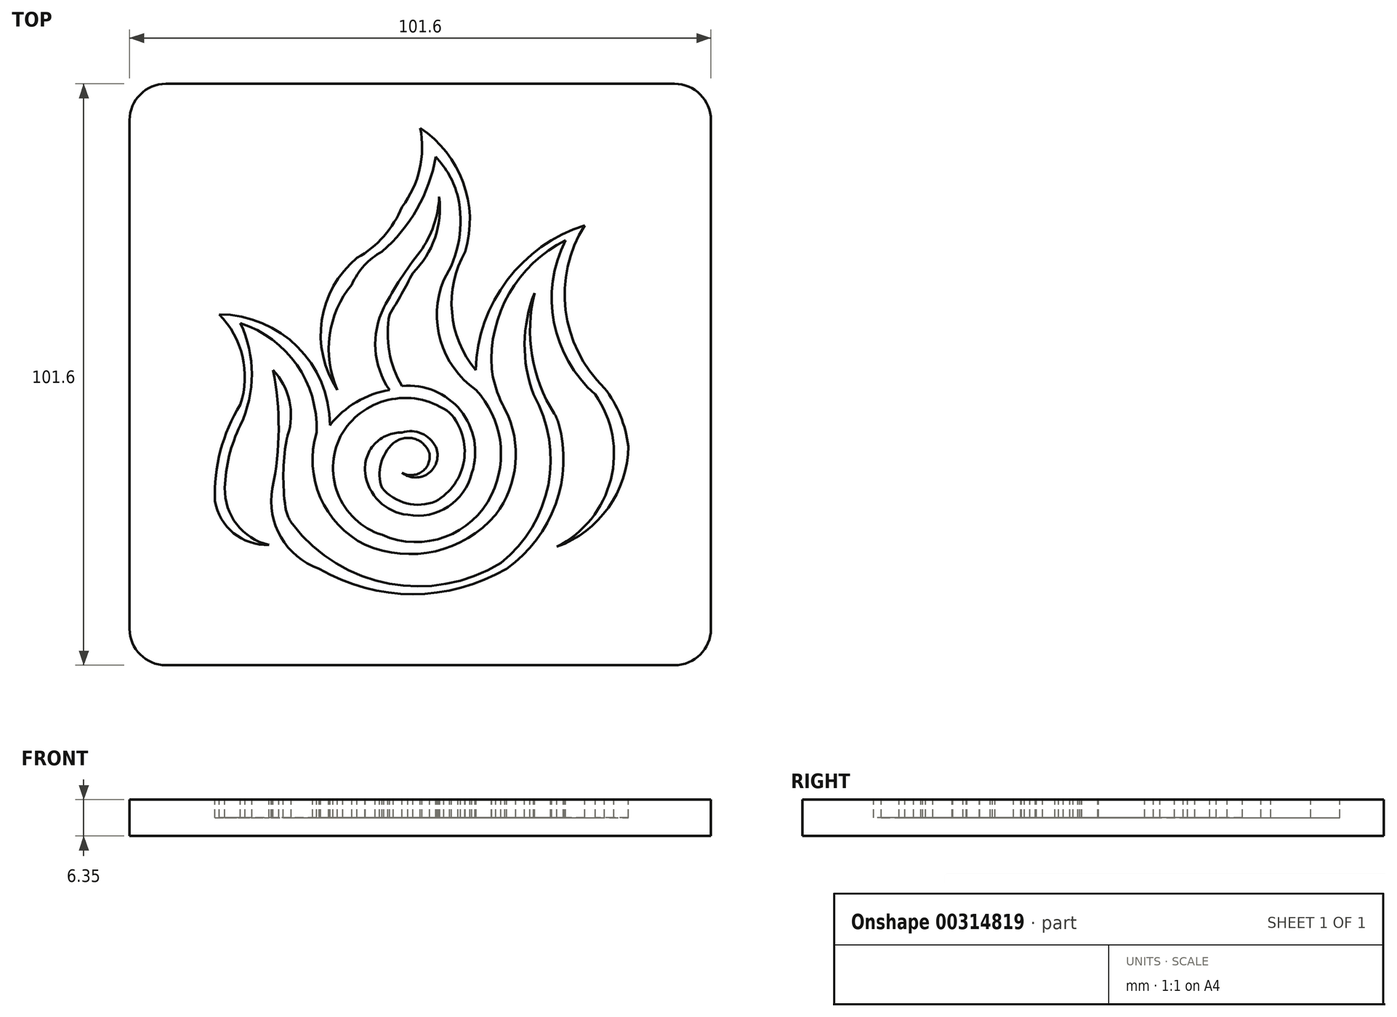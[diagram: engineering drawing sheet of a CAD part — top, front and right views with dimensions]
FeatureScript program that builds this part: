
annotation { "Feature Type Name" : "Feature", "Feature Type Description" : "" }
export const myFeature = defineFeature(function(context is Context, id is Id, definition is map)
    precondition{}
    {
        {
            var Q0;
            Q0=qCreatedBy(makeId("Top.planeOp"),FACE);
            var sketch = newSketch(context, id + "F0", { "sketchPlane" : qUnion([Q0])});
            skLineSegment(sketch, "E0.bottom", {"start": v(-44.45, 50.8) * mm, "end": v(44.45, 50.8) * mm});
            skLineSegment(sketch, "E0.top", {"start": v(-44.45, -50.8) * mm, "end": v(44.45, -50.8) * mm});
            skLineSegment(sketch, "E0.left", {"start": v(-50.8, 44.45) * mm, "end": v(-50.8, -44.45) * mm});
            skLineSegment(sketch, "E0.right", {"start": v(50.8, 44.45) * mm, "end": v(50.8, -44.45) * mm});
            skPoint(sketch, "E1.visualSharp", {"position": v(-50.8, 50.8) * mm});
            skArc(sketch, "E1.filletArc", {"start": v(-44.45, 50.8) * mm, "mid": v(-48.94, 48.94) * mm, "end": v(-50.8, 44.45) * mm});
            skPoint(sketch, "E2.visualSharp", {"position": v(50.8, 50.8) * mm});
            skArc(sketch, "E2.filletArc", {"start": v(50.8, 44.45) * mm, "mid": v(48.94, 48.94) * mm, "end": v(44.45, 50.8) * mm});
            skPoint(sketch, "E3.visualSharp", {"position": v(50.8, -50.8) * mm});
            skArc(sketch, "E3.filletArc", {"start": v(44.45, -50.8) * mm, "mid": v(48.94, -48.94) * mm, "end": v(50.8, -44.45) * mm});
            skPoint(sketch, "E4.visualSharp", {"position": v(-50.8, -50.8) * mm});
            skArc(sketch, "E4.filletArc", {"start": v(-50.8, -44.45) * mm, "mid": v(-48.94, -48.94) * mm, "end": v(-44.45, -50.8) * mm});
            skSolve(sketch);
        }
        {
            var Q0;
            Q0 = qSketchRegion(id + "F0", true);
            extrude(context, id + "F1", {"entities" : qUnion([Q0]), "depth" : 6.35 * mm});
        }
        {
            var Q0;
            Q0=makeQuery(id+"F1.opExtrude","CAP_FACE",FACE,{"disambiguationData":[OSD([sQuery(id+"F0.wireOp",EDGE,"E0.bottom"),sQuery(id+"F0.wireOp",EDGE,"E0.top"),sQuery(id+"F0.wireOp",EDGE,"E0.left"),sQuery(id+"F0.wireOp",EDGE,"E0.right"),sQuery(id+"F0.wireOp",EDGE,"E1.filletArc"),sQuery(id+"F0.wireOp",EDGE,"E2.filletArc"),sQuery(id+"F0.wireOp",EDGE,"E3.filletArc"),sQuery(id+"F0.wireOp",EDGE,"E4.filletArc")])],"isStart":false});
            var sketch = newSketch(context, id + "F2", { "sketchPlane" : qUnion([Q0])});
            skArc(sketch, "E5", {"start": v(23.87, -30.1) * mm, "mid": v(32.86, -23.28) * mm, "end": v(36.36, -12.54) * mm});
            skArc(sketch, "E6", {"start": v(36.36, -12.54) * mm, "mid": v(34.97, -7.17) * mm, "end": v(32.2, -2.37) * mm});
            skArc(sketch, "E7", {"start": v(28.74, 26.08) * mm, "mid": v(25.4, 11.24) * mm, "end": v(32.2, -2.37) * mm});
            skArc(sketch, "E8", {"start": v(28.74, 26.08) * mm, "mid": v(15.18, 16.47) * mm, "end": v(9.68, 0.79) * mm});
            skArc(sketch, "E9", {"start": v(25.4, 23.44) * mm, "mid": v(15.54, 14.16) * mm, "end": v(12.48, 0.96) * mm});
            skPoint(sketch, "E9.startSnap0", {"position": v(25.4, 11.24) * mm});
            skArc(sketch, "E10", {"start": v(25.4, 23.44) * mm, "mid": v(23.37, 9.08) * mm, "end": v(30.59, -3.5) * mm});
            skArc(sketch, "E11", {"start": v(23.87, -30.1) * mm, "mid": v(33.3, -18.33) * mm, "end": v(30.59, -3.5) * mm});
            skArc(sketch, "E12", {"start": v(19.97, 14.22) * mm, "mid": v(18.23, 5.38) * mm, "end": v(19.79, -3.5) * mm});
            skArc(sketch, "E13", {"start": v(19.97, 14.22) * mm, "mid": v(19.53, 3.35) * mm, "end": v(23.41, -6.81) * mm});
            skArc(sketch, "E14", {"start": v(15.08, -33.93) * mm, "mid": v(23.66, -22.67) * mm, "end": v(24.18, -8.53) * mm});
            skArc(sketch, "E15", {"start": v(14.08, -32.93) * mm, "mid": v(22.37, -19.27) * mm, "end": v(19.79, -3.5) * mm});
            skArc(sketch, "E16", {"start": v(-17.68, -33.93) * mm, "mid": v(-1.3, -38.39) * mm, "end": v(15.08, -33.93) * mm});
            skArc(sketch, "E17", {"start": v(-22.32, -26.15) * mm, "mid": v(-5.42, -36.55) * mm, "end": v(14.08, -32.93) * mm});
            skArc(sketch, "E18", {"start": v(-25.83, -19.9) * mm, "mid": v(-24.35, -28.42) * mm, "end": v(-17.68, -33.93) * mm});
            skArc(sketch, "E19", {"start": v(-23.4, -11.57) * mm, "mid": v(-23.93, -17.38) * mm, "end": v(-23.56, -23.2) * mm});
            skArc(sketch, "E20", {"start": v(-23.16, -10.65) * mm, "mid": v(-22.87, -4.58) * mm, "end": v(-25.74, 0.79) * mm});
            skArc(sketch, "E21", {"start": v(-25.83, -19.9) * mm, "mid": v(-24.74, -9.56) * mm, "end": v(-25.74, 0.79) * mm});
            skPoint(sketch, "E22.visualSharp", {"position": v(-23.3, -24.79) * mm});
            skArc(sketch, "E22.filletArc", {"start": v(-23.56, -23.2) * mm, "mid": v(-23.13, -24.75) * mm, "end": v(-22.32, -26.15) * mm});
            skPoint(sketch, "E23.visualSharp", {"position": v(-23.3, -11.03) * mm});
            skArc(sketch, "E23.filletArc", {"start": v(-23.16, -10.65) * mm, "mid": v(-23.3, -11.1) * mm, "end": v(-23.4, -11.57) * mm});
            skPoint(sketch, "E24.visualSharp", {"position": v(23.87, -7.5) * mm});
            skArc(sketch, "E24.filletArc", {"start": v(24.18, -8.53) * mm, "mid": v(23.86, -7.64) * mm, "end": v(23.41, -6.81) * mm});
            skArc(sketch, "E25", {"start": v(-35.88, -22.07) * mm, "mid": v(-32.63, -27.7) * mm, "end": v(-26.46, -29.77) * mm});
            skArc(sketch, "E26", {"start": v(-34.16, -19.81) * mm, "mid": v(-32.09, -26.16) * mm, "end": v(-26.46, -29.77) * mm});
            skArc(sketch, "E27", {"start": v(-31.44, -5.24) * mm, "mid": v(-34.91, -13.33) * mm, "end": v(-35.88, -22.07) * mm});
            skArc(sketch, "E28", {"start": v(-31.44, -8.86) * mm, "mid": v(-33.39, -14.19) * mm, "end": v(-34.16, -19.81) * mm});
            skArc(sketch, "E29", {"start": v(-31.44, -8.86) * mm, "mid": v(-29.43, 0.06) * mm, "end": v(-31.44, 8.97) * mm});
            skArc(sketch, "E30", {"start": v(-31.44, -5.24) * mm, "mid": v(-31.06, 3.16) * mm, "end": v(-35.15, 10.5) * mm});
            skArc(sketch, "E31", {"start": v(-15.78, -8.86) * mm, "mid": v(-21.46, 4.83) * mm, "end": v(-35.15, 10.5) * mm});
            skArc(sketch, "E32", {"start": v(-18.14, -10.13) * mm, "mid": v(-21.57, 1.67) * mm, "end": v(-31.44, 8.97) * mm});
            skArc(sketch, "E33", {"start": v(-18.14, -10.13) * mm, "mid": v(-17.46, -21.5) * mm, "end": v(-9.63, -29.77) * mm});
            skArc(sketch, "E34", {"start": v(-9.63, -29.77) * mm, "mid": v(2.64, -30.88) * mm, "end": v(13.18, -24.52) * mm});
            skArc(sketch, "E35", {"start": v(13.18, -24.52) * mm, "mid": v(16.64, -15.52) * mm, "end": v(14.8, -6.05) * mm});
            skArc(sketch, "E36", {"start": v(12.48, 0.96) * mm, "mid": v(13.31, -2.66) * mm, "end": v(14.8, -6.05) * mm});
            skArc(sketch, "E37", {"start": v(-5.38, -2.7) * mm, "mid": v(-11.16, -4.8) * mm, "end": v(-15.78, -8.86) * mm});
            skArc(sketch, "E38", {"start": v(-6.37, 11.69) * mm, "mid": v(-7.84, 4.35) * mm, "end": v(-5.38, -2.7) * mm});
            skArc(sketch, "E39", {"start": v(0, 21.49) * mm, "mid": v(-3.41, 16.73) * mm, "end": v(-6.37, 11.69) * mm});
            skArc(sketch, "E40", {"start": v(0, 21.49) * mm, "mid": v(2.35, 26.03) * mm, "end": v(3.31, 31.06) * mm});
            skArc(sketch, "E41", {"start": v(-1.3, 17.75) * mm, "mid": v(2.56, 23.86) * mm, "end": v(3.31, 31.06) * mm});
            skArc(sketch, "E42", {"start": v(-5.38, 10.5) * mm, "mid": v(-3.26, 14.08) * mm, "end": v(-1.3, 17.75) * mm});
            skArc(sketch, "E43", {"start": v(-5.38, 10.5) * mm, "mid": v(-5.42, 4.04) * mm, "end": v(-3.18, -2.04) * mm});
            skArc(sketch, "E44", {"start": v(9.02, -17.17) * mm, "mid": v(7.04, -6.28) * mm, "end": v(-3.18, -2.04) * mm});
            skArc(sketch, "E45", {"start": v(-2.2, -24.52) * mm, "mid": v(4.88, -23.09) * mm, "end": v(9.02, -17.17) * mm});
            skArc(sketch, "E46", {"start": v(-9.63, -17.17) * mm, "mid": v(-7.2, -22.16) * mm, "end": v(-2.2, -24.52) * mm});
            skArc(sketch, "E47", {"start": v(-3.18, -10.13) * mm, "mid": v(-8, -12.18) * mm, "end": v(-9.63, -17.17) * mm});
            skArc(sketch, "E48", {"start": v(2.7, -12.64) * mm, "mid": v(0.22, -10.3) * mm, "end": v(-3.18, -10.13) * mm});
            skArc(sketch, "E49", {"start": v(-3.18, -17.17) * mm, "mid": v(1.52, -17.2) * mm, "end": v(2.7, -12.64) * mm});
            skArc(sketch, "E50", {"start": v(-3.18, -17.17) * mm, "mid": v(0.24, -17.02) * mm, "end": v(1.63, -13.89) * mm});
            skArc(sketch, "E51", {"start": v(1.63, -13.89) * mm, "mid": v(-1.03, -11.23) * mm, "end": v(-4.7, -12) * mm});
            skArc(sketch, "E52", {"start": v(-4.7, -12) * mm, "mid": v(-6.89, -15.6) * mm, "end": v(-6.7, -19.81) * mm});
            skArc(sketch, "E53", {"start": v(-6.7, -19.81) * mm, "mid": v(-2.38, -22.5) * mm, "end": v(2.7, -22.15) * mm});
            skArc(sketch, "E54", {"start": v(2.7, -22.15) * mm, "mid": v(7.65, -15) * mm, "end": v(5.14, -6.69) * mm});
            skArc(sketch, "E55", {"start": v(5.14, -6.69) * mm, "mid": v(-4.96, -4.31) * mm, "end": v(-13.56, -10.13) * mm});
            skArc(sketch, "E56", {"start": v(-13.56, -10.13) * mm, "mid": v(-14.43, -20.72) * mm, "end": v(-6.7, -28.01) * mm});
            skArc(sketch, "E57", {"start": v(-6.7, -28.01) * mm, "mid": v(4.33, -28.39) * mm, "end": v(12.48, -20.95) * mm});
            skArc(sketch, "E58", {"start": v(12.48, -20.95) * mm, "mid": v(13.93, -11.4) * mm, "end": v(9.74, -2.7) * mm});
            skArc(sketch, "E59", {"start": v(4.1, 16.5) * mm, "mid": v(3.56, 5.91) * mm, "end": v(9.74, -2.7) * mm});
            skArc(sketch, "E60", {"start": v(7.88, 21.49) * mm, "mid": v(5.54, 10.85) * mm, "end": v(9.68, 0.79) * mm});
            skArc(sketch, "E61", {"start": v(4.1, 16.5) * mm, "mid": v(6.76, 23.53) * mm, "end": v(6.57, 31.06) * mm});
            skArc(sketch, "E62", {"start": v(7.88, 21.49) * mm, "mid": v(7.5, 33.58) * mm, "end": v(0, 43.09) * mm});
            skArc(sketch, "E63", {"start": v(6.57, 31.06) * mm, "mid": v(5.1, 34.8) * mm, "end": v(2.7, 38.03) * mm});
            skArc(sketch, "E64", {"start": v(-3.18, 29.3) * mm, "mid": v(-0.12, 35.86) * mm, "end": v(0, 43.09) * mm});
            skArc(sketch, "E65", {"start": v(-6.7, 21.49) * mm, "mid": v(-0.56, 28.94) * mm, "end": v(2.7, 38.03) * mm});
            skArc(sketch, "E66", {"start": v(-6.7, 21.49) * mm, "mid": v(-9.8, 19.04) * mm, "end": v(-11.96, 15.73) * mm});
            skArc(sketch, "E67", {"start": v(-11.96, 15.73) * mm, "mid": v(-15.83, 6.87) * mm, "end": v(-14.47, -2.7) * mm});
            skArc(sketch, "E68", {"start": v(-11.05, 20.38) * mm, "mid": v(-6.36, 24.17) * mm, "end": v(-3.18, 29.3) * mm});
            skArc(sketch, "E69", {"start": v(-11.05, 20.38) * mm, "mid": v(-17.2, 9.5) * mm, "end": v(-14.47, -2.7) * mm});
            skSolve(sketch);
        }
        {
            var Q0;
            Q0 = qSketchRegion(id + "F2", true);
            extrude(context, id + "F3", {"entities" : qUnion([Q0]), "operationType" : NewBodyOperationType.REMOVE, "oppositeDirection" : true, "depth" : 3.17 * mm});
        }
    });
